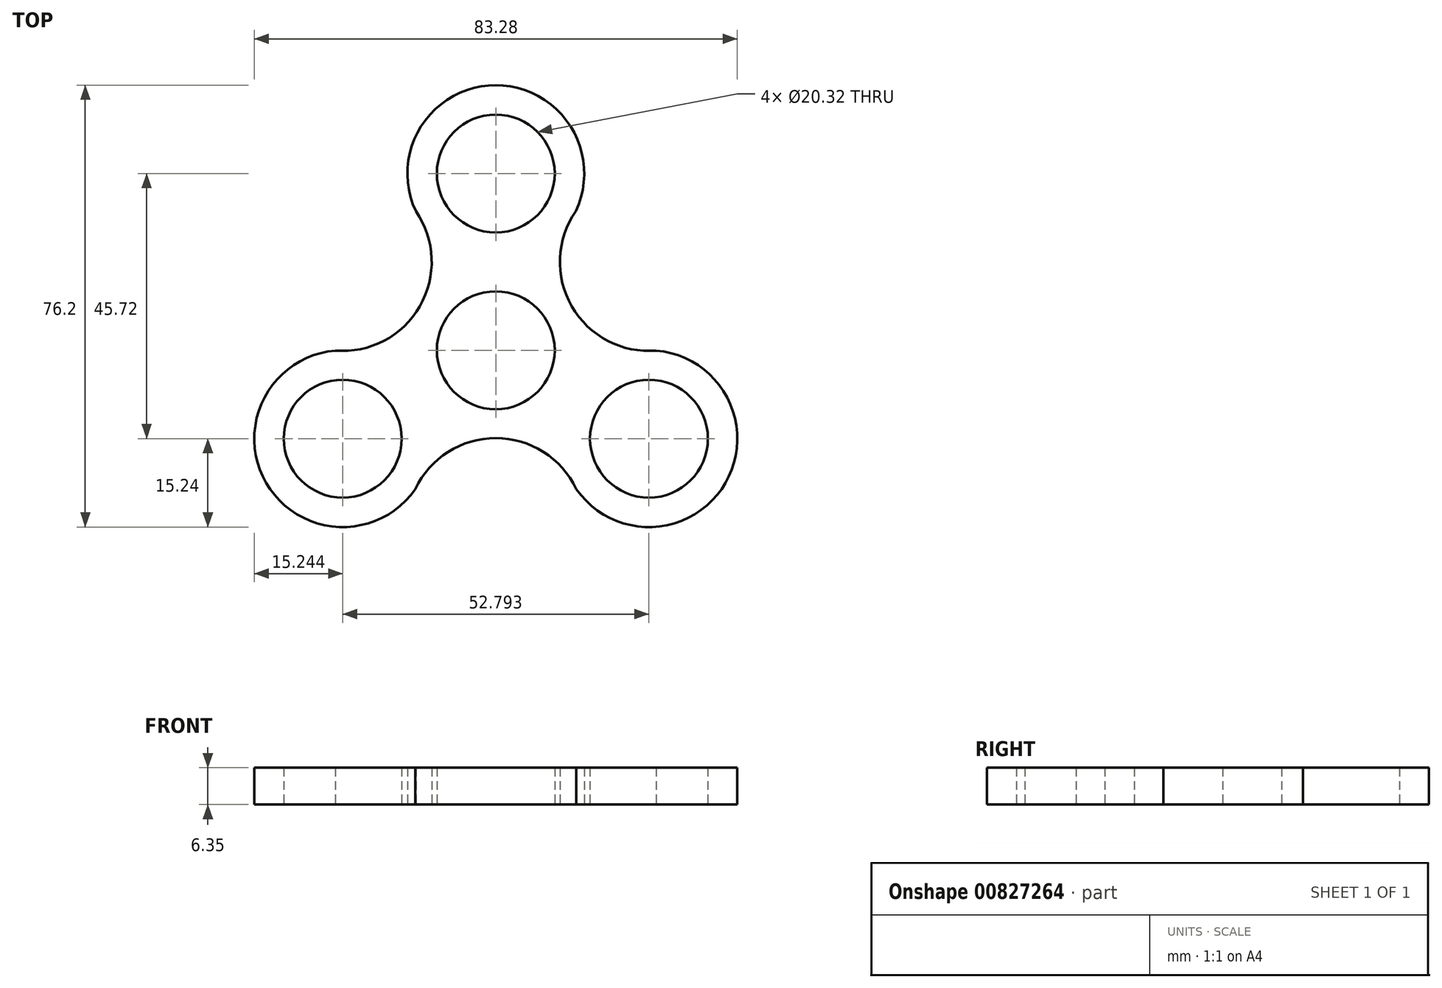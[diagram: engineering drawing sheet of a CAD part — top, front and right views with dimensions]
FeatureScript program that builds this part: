
annotation { "Feature Type Name" : "Feature", "Feature Type Description" : "" }
export const myFeature = defineFeature(function(context is Context, id is Id, definition is map)
    precondition{}
    {
        {
            var Q0;
            Q0=qCreatedBy(makeId("Top.planeOp"),FACE);
            var sketch = newSketch(context, id + "F0", { "sketchPlane" : qUnion([Q0])});
            skCircle(sketch, "E0", {"center": v(0, 0) * mm, "radius": 10.16 * mm});
            skCircle(sketch, "E1", {"center": v(0, 30.48) * mm, "radius": 10.16 * mm});
            skArc(sketch, "E2", {"start": v(12.52, 21.78) * mm, "mid": v(0, 45.72) * mm, "end": v(-12.52, 21.78) * mm});
            skCircle(sketch, "E3.1.0", {"center": v(-26.4, -15.24) * mm, "radius": 10.16 * mm});
            skArc(sketch, "E3.1.1", {"start": v(-25.12, -0.05) * mm, "mid": v(-39.6, -22.86) * mm, "end": v(-12.6, -21.73) * mm});
            skCircle(sketch, "E3.2.0", {"center": v(26.4, -15.24) * mm, "radius": 10.16 * mm});
            skArc(sketch, "E3.2.1", {"start": v(12.6, -21.73) * mm, "mid": v(39.6, -22.86) * mm, "end": v(25.12, -0.05) * mm});
            skArc(sketch, "E4", {"start": v(-27.67, -0.05) * mm, "mid": v(-13.1, 7.57) * mm, "end": v(-13.79, 23.99) * mm});
            skArc(sketch, "E5.1.0", {"start": v(13.88, -23.94) * mm, "mid": v(0, -15.13) * mm, "end": v(-13.88, -23.94) * mm});
            skArc(sketch, "E5.2.0", {"start": v(13.79, 23.99) * mm, "mid": v(13.1, 7.57) * mm, "end": v(27.67, -0.05) * mm});
            skLineSegment(sketch, "E6.trimOffspring", {"start": v(-12.1, 6.98) * mm, "end": v(-13.1, 7.57) * mm});
            skSolve(sketch);
        }
        {
            var Q0;
            Q0=makeQuery(id+"F0.imprint","IMPRINT",FACE,{"disambiguationData":[TD([[makeQuery(id+"F0.imprint","IMPRINT",EDGE,{"derivedFrom":sQuery(id+"F0.wireOp",EDGE,"E0")}),-1.0]])]});
            extrude(context, id + "F1", {"entities" : qUnion([Q0]), "depth" : 6.35 * mm, "offsetDistance" : 25.4 * mm});
        }
    });
